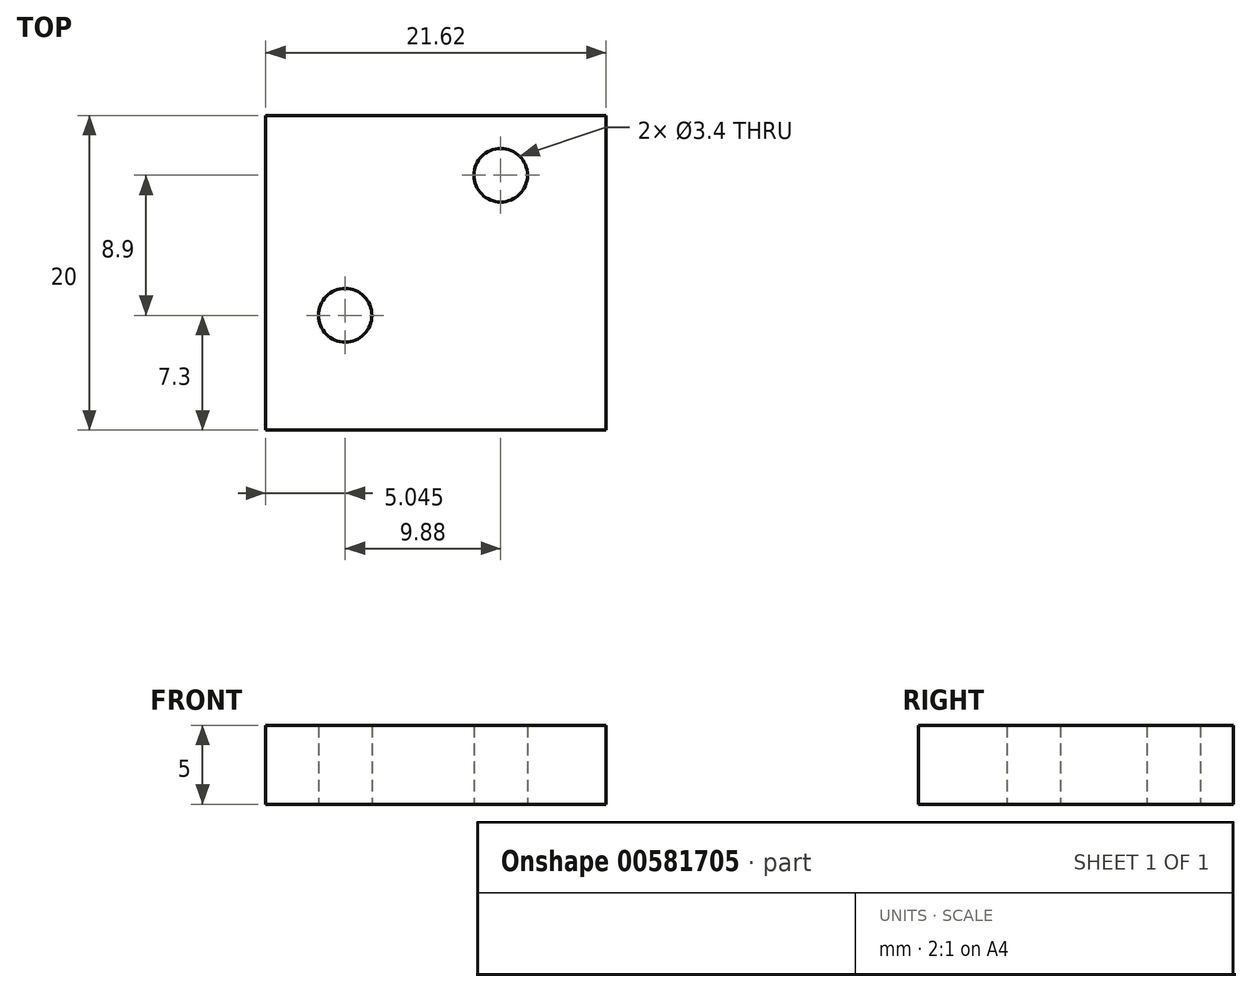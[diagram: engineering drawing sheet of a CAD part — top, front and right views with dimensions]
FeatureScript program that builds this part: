
annotation { "Feature Type Name" : "Feature", "Feature Type Description" : "" }
export const myFeature = defineFeature(function(context is Context, id is Id, definition is map)
    precondition{}
    {
        {
            var Q0;
            Q0=qCreatedBy(makeId("Top.planeOp"),FACE);
            var sketch = newSketch(context, id + "F0", { "sketchPlane" : qUnion([Q0])});
            skLineSegment(sketch, "E0.bottom", {"start": v(-10.81, 10) * mm, "end": v(10.82, 10) * mm});
            skLineSegment(sketch, "E0.top", {"start": v(-10.82, -10) * mm, "end": v(10.81, -10) * mm});
            skLineSegment(sketch, "E0.left", {"start": v(-10.81, 10) * mm, "end": v(-10.82, -10) * mm});
            skLineSegment(sketch, "E0.right", {"start": v(10.82, 10) * mm, "end": v(10.81, -10) * mm});
            skPoint(sketch, "E0.middle", {"position": v(0, 0) * mm});
            skCircle(sketch, "E1", {"center": v(4.12, 6.2) * mm, "radius": 1.7 * mm});
            skCircle(sketch, "E2", {"center": v(-5.77, -2.7) * mm, "radius": 1.7 * mm});
            skSolve(sketch);
        }
        {
            var Q0;
            Q0=makeQuery(id+"F0.imprint","IMPRINT",FACE,{"disambiguationData":[TD([[makeQuery(id+"F0.imprint","IMPRINT",EDGE,{"derivedFrom":sQuery(id+"F0.wireOp",EDGE,"E0.bottom")}),-1.0]])]});
            extrude(context, id + "F1", {"entities" : qUnion([Q0]), "depth" : 5 * mm, "offsetDistance" : 25 * mm});
        }
    });
